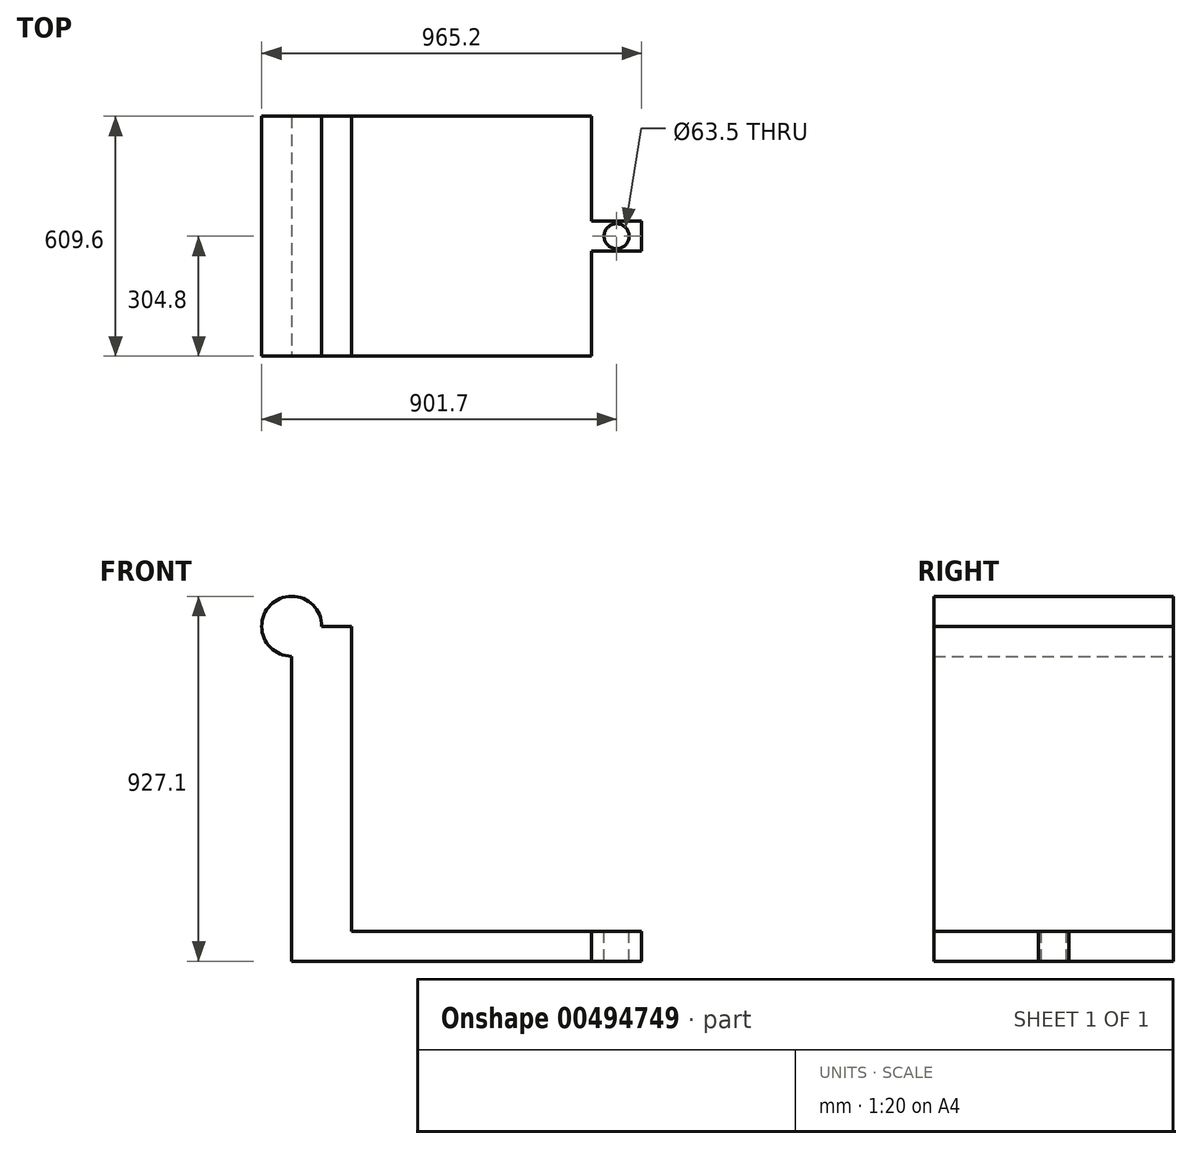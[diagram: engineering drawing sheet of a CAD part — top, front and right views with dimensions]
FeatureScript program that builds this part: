
annotation { "Feature Type Name" : "Feature", "Feature Type Description" : "" }
export const myFeature = defineFeature(function(context is Context, id is Id, definition is map)
    precondition{}
    {
        {
            var Q0;
            Q0=qCreatedBy(makeId("Right.planeOp"),FACE);
            var sketch = newSketch(context, id + "F0", { "sketchPlane" : qUnion([Q0])});
            skLineSegment(sketch, "E0.bottom", {"start": v(304.8, -425.45) * mm, "end": v(-304.8, -425.45) * mm});
            skLineSegment(sketch, "E0.top", {"start": v(304.8, 425.45) * mm, "end": v(-304.8, 425.45) * mm});
            skLineSegment(sketch, "E0.left", {"start": v(304.8, -425.45) * mm, "end": v(304.8, 425.45) * mm});
            skLineSegment(sketch, "E0.right", {"start": v(-304.8, -425.45) * mm, "end": v(-304.8, 425.45) * mm});
            skPoint(sketch, "E0.middle", {"position": v(0, 0) * mm});
            skSolve(sketch);
        }
        {
            var Q0;
            Q0=makeQuery(id+"F0.imprint","IMPRINT",FACE,{"disambiguationData":[TD([[makeQuery(id+"F0.imprint","IMPRINT",EDGE,{"derivedFrom":sQuery(id+"F0.wireOp",EDGE,"E0.bottom")}),-1.0]])]});
            extrude(context, id + "F1", {"entities" : qUnion([Q0]), "depth" : 152.4 * mm});
        }
        {
            var Q0;
            Q0=makeQuery(id+"F1.opExtrude","CAP_FACE",FACE,{"disambiguationData":[OSD([sQuery(id+"F0.wireOp",EDGE,"E0.bottom"),sQuery(id+"F0.wireOp",EDGE,"E0.top"),sQuery(id+"F0.wireOp",EDGE,"E0.left"),sQuery(id+"F0.wireOp",EDGE,"E0.right")])],"isStart":false});
            var sketch = newSketch(context, id + "F2", { "sketchPlane" : qUnion([Q0])});
            skLineSegment(sketch, "E1.bottom", {"start": v(-304.8, -425.45) * mm, "end": v(304.8, -425.45) * mm});
            skLineSegment(sketch, "E1.top", {"start": v(-304.8, -349.25) * mm, "end": v(304.8, -349.25) * mm});
            skLineSegment(sketch, "E1.left", {"start": v(-304.8, -425.45) * mm, "end": v(-304.8, -349.25) * mm});
            skLineSegment(sketch, "E1.right", {"start": v(304.8, -425.45) * mm, "end": v(304.8, -349.25) * mm});
            skSolve(sketch);
        }
        {
            var Q0;
            Q0 = qSketchRegion(id + "F2", true);
            extrude(context, id + "F3", {"entities" : qUnion([Q0]), "operationType" : NewBodyOperationType.ADD, "depth" : 609.6 * mm});
        }
        {
            var Q0;
            Q0=makeQuery(id+"F3.opExtrude","CAP_FACE",FACE,{"disambiguationData":[OSD([sQuery(id+"F2.wireOp",EDGE,"E1.bottom"),sQuery(id+"F2.wireOp",EDGE,"E1.top"),sQuery(id+"F2.wireOp",EDGE,"E1.left"),sQuery(id+"F2.wireOp",EDGE,"E1.right")])],"isStart":false});
            var sketch = newSketch(context, id + "F4", { "sketchPlane" : qUnion([Q0])});
            skPoint(sketch, "E2.endSnap0", {"position": v(0, -349.25) * mm});
            skLineSegment(sketch, "E3.bottom", {"start": v(38.1, -425.45) * mm, "end": v(-38.1, -425.45) * mm});
            skLineSegment(sketch, "E3.top", {"start": v(38.1, -349.25) * mm, "end": v(-38.1, -349.25) * mm});
            skLineSegment(sketch, "E3.left", {"start": v(38.1, -425.45) * mm, "end": v(38.1, -349.25) * mm});
            skLineSegment(sketch, "E3.right", {"start": v(-38.1, -425.45) * mm, "end": v(-38.1, -349.25) * mm});
            skPoint(sketch, "E3.middle", {"position": v(0, -387.35) * mm});
            skSolve(sketch);
        }
        {
            var Q0;
            Q0 = qSketchRegion(id + "F4", true);
            extrude(context, id + "F5", {"entities" : qUnion([Q0]), "operationType" : NewBodyOperationType.ADD, "depth" : 127 * mm});
        }
        {
            var Q0;
            Q0=makeQuery(id+"F5.boolean.opBoolean","MERGE",FACE,{"derivedFrom":[makeQuery(id+"F3.opExtrude","SWEPT_FACE",FACE,{"disambiguationData":[OSD([sQuery(id+"F2.wireOp",EDGE,"E1.top")])]}),makeQuery(id+"F5.opExtrude","SWEPT_FACE",FACE,{"disambiguationData":[OSD([sQuery(id+"F4.wireOp",EDGE,"E3.top")])]})]});
            var sketch = newSketch(context, id + "F6", { "sketchPlane" : qUnion([Q0])});
            skCircle(sketch, "E4", {"center": v(825.5, 0) * mm, "radius": 31.75 * mm});
            skPoint(sketch, "E4.centerSnap0", {"position": v(825.5, 38.1) * mm});
            skSolve(sketch);
        }
        {
            var Q0;
            Q0 = qSketchRegion(id + "F6", true);
            extrude(context, id + "F7", {"entities" : qUnion([Q0]), "operationType" : NewBodyOperationType.REMOVE, "oppositeDirection" : true, "depth" : 137.16 * mm});
        }
        {
            var Q0;
            Q0=makeQuery(id+"F1.opExtrude","SWEPT_FACE",FACE,{"disambiguationData":[OSD([sQuery(id+"F0.wireOp",EDGE,"E0.top")])]});
            var sketch = newSketch(context, id + "F8", { "sketchPlane" : qUnion([Q0])});
            skLineSegment(sketch, "E5.bottom", {"start": v(0, 304.8) * mm, "end": v(76.2, 304.8) * mm});
            skLineSegment(sketch, "E5.top", {"start": v(0, -304.8) * mm, "end": v(76.2, -304.8) * mm});
            skLineSegment(sketch, "E5.left", {"start": v(0, 304.8) * mm, "end": v(0, -304.8) * mm});
            skLineSegment(sketch, "E5.right", {"start": v(76.2, 304.8) * mm, "end": v(76.2, -304.8) * mm});
            skSolve(sketch);
        }
        {
            var Q0;
            Q0 = qSketchRegion(id + "F8", true);
            var Q1;
            Q1=sQuery(id+"F8.wireOp",EDGE,"E5.left");
            revolve(context, id + "F9", {"operationType" : NewBodyOperationType.ADD, "entities" : qUnion([Q0]), "axis" : qUnion([Q1]), "revolveType" : RevolveType.FULL});
        }
    });
